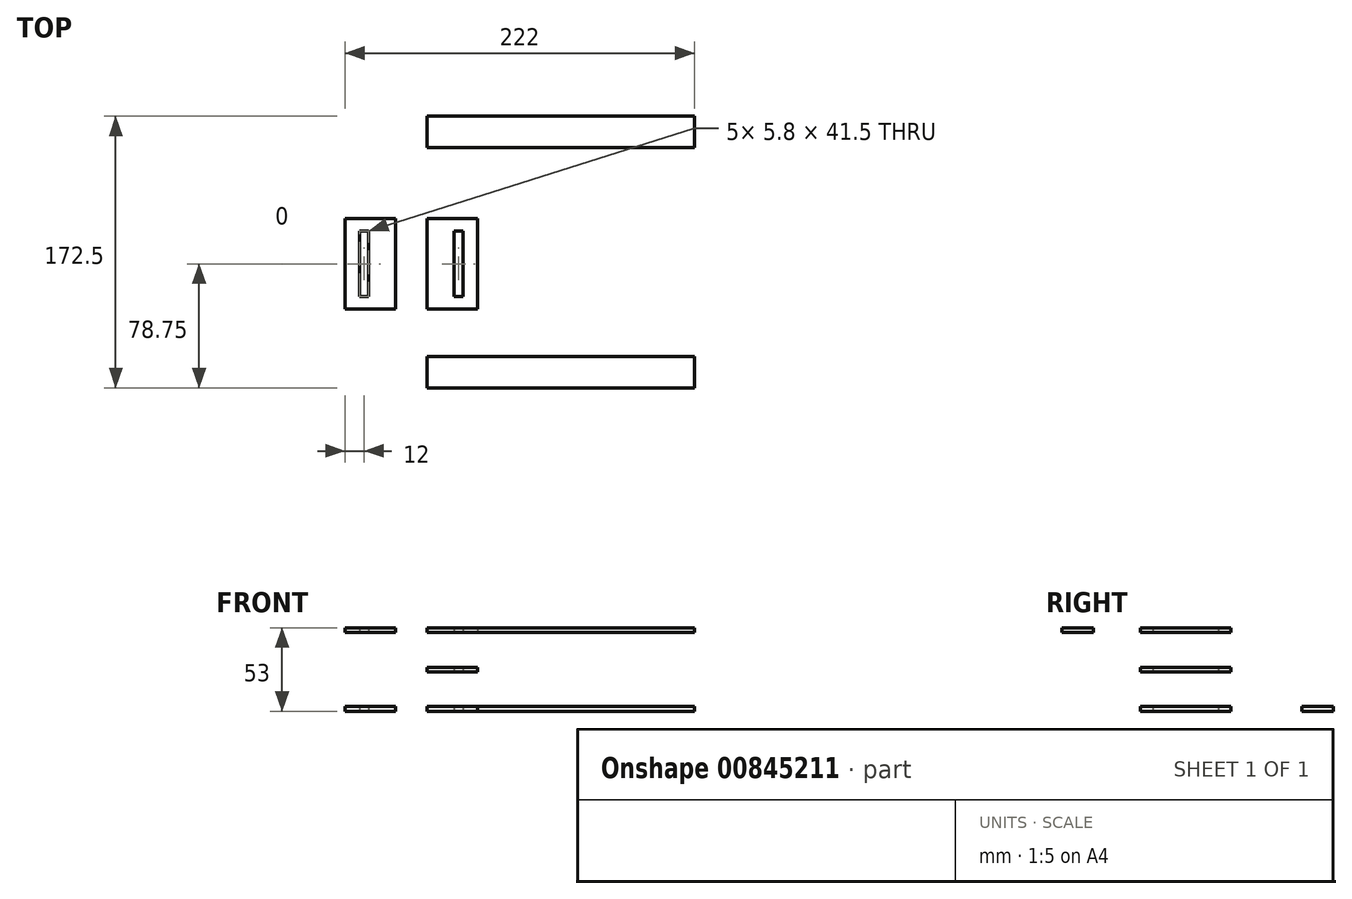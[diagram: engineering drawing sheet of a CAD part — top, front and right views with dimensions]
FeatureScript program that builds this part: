
annotation { "Feature Type Name" : "Feature", "Feature Type Description" : "" }
export const myFeature = defineFeature(function(context is Context, id is Id, definition is map)
    precondition{}
    {
        {
            var Q0;
            Q0=qCreatedBy(makeId("Top.planeOp"),FACE);
            var sketch = newSketch(context, id + "F0", { "sketchPlane" : qUnion([Q0])});
            skLineSegment(sketch, "E0.bottom", {"start": v(2.9, 20.75) * mm, "end": v(-2.9, 20.75) * mm});
            skLineSegment(sketch, "E0.top", {"start": v(2.9, -20.75) * mm, "end": v(-2.9, -20.75) * mm});
            skLineSegment(sketch, "E0.left", {"start": v(2.9, 20.75) * mm, "end": v(2.9, -20.75) * mm});
            skLineSegment(sketch, "E0.right", {"start": v(-2.9, 20.75) * mm, "end": v(-2.9, -20.75) * mm});
            skPoint(sketch, "E0.middle", {"position": v(0, 0) * mm});
            skLineSegment(sketch, "E1.top", {"start": v(-20, 28.75) * mm, "end": v(12, 28.75) * mm});
            skLineSegment(sketch, "E1.left", {"start": v(-20, -28.75) * mm, "end": v(-20, 28.75) * mm});
            skLineSegment(sketch, "E1.right", {"start": v(12, -28.75) * mm, "end": v(12, 28.75) * mm});
            skLineSegment(sketch, "E2.bottom", {"start": v(-20, -28.75) * mm, "end": v(12, -28.75) * mm});
            skSolve(sketch);
        }
        {
            var Q0;
            Q0=makeQuery(id+"F0.imprint","IMPRINT",FACE,{"disambiguationData":[TD([[makeQuery(id+"F0.imprint","IMPRINT",EDGE,{"derivedFrom":sQuery(id+"F0.wireOp",EDGE,"E0.bottom")}),-1.0]])]});
            var Q1;
            Q1=makeQuery(id+"F0.imprint","IMPRINT",FACE,{"disambiguationData":[TD([[makeQuery(id+"F0.imprint","IMPRINT",EDGE,{"derivedFrom":sQuery(id+"F0.wireOp",EDGE,"JnjF8kHf-qQj9-1dLX-JmeW-Ht2cM5oFc9sg.bottom")}),1.0]])]});
            var Q2;
            {var subQ0=sQuery(id+"F0.wireOp",EDGE,"E2.bottom");Q2=makeQuery(id+"F0.imprint","IMPRINT",FACE,{"disambiguationData":[TD([[makeQuery(id+"F0.imprint","IMPRINT",EDGE,{"derivedFrom":subQ0}),1.0]])]});}
            extrude(context, id + "F1", {"entities" : qUnion([Q0, Q1, Q2]), "depth" : 3 * mm, "offsetDistance" : 25 * mm});
        }
        {
            var Q0;
            Q0=qCreatedBy(makeId("Top.planeOp"),FACE);
            cPlane(context, id + "F2", {"entities" : qUnion([Q0]), "cplaneType" : CPlaneType.OFFSET, "offset" : 25 * mm, "width" : 150 * mm, "height" : 150 * mm});
        }
        {
            var Q0;
            Q0=qCreatedBy(id+"F2.planeOp",FACE);
            var sketch = newSketch(context, id + "F3", { "sketchPlane" : qUnion([Q0])});
            skLineSegment(sketch, "E3.0.0", {"start": v(-20, 28.75) * mm, "end": v(-20, -28.75) * mm});
            skLineSegment(sketch, "E3.0.1", {"start": v(-20, -28.75) * mm, "end": v(12, -28.75) * mm});
            skLineSegment(sketch, "E3.0.2", {"start": v(12, -28.75) * mm, "end": v(12, 28.75) * mm});
            skLineSegment(sketch, "E3.0.3", {"start": v(12, 28.75) * mm, "end": v(-20, 28.75) * mm});
            skLineSegment(sketch, "E4.0", {"start": v(-2.9, 20.75) * mm, "end": v(-2.9, -20.75) * mm});
            skLineSegment(sketch, "E4.1", {"start": v(2.9, 20.75) * mm, "end": v(-2.9, 20.75) * mm});
            skLineSegment(sketch, "E4.2", {"start": v(2.9, 20.75) * mm, "end": v(2.9, -20.75) * mm});
            skLineSegment(sketch, "E4.3", {"start": v(2.9, -20.75) * mm, "end": v(-2.9, -20.75) * mm});
            skLineSegment(sketch, "E5.bottom", {"start": v(-20, -28.75) * mm, "end": v(0, -28.75) * mm});
            skLineSegment(sketch, "E5.top", {"start": v(-20, -58.75) * mm, "end": v(0, -58.75) * mm});
            skLineSegment(sketch, "E5.left", {"start": v(-20, -28.75) * mm, "end": v(-20, -58.75) * mm});
            skLineSegment(sketch, "E5.right", {"start": v(0, -28.75) * mm, "end": v(0, -58.75) * mm});
            skLineSegment(sketch, "E6.bottom", {"start": v(-20, -58.75) * mm, "end": v(150, -58.75) * mm});
            skLineSegment(sketch, "E6.top", {"start": v(-20, -78.75) * mm, "end": v(150, -78.75) * mm});
            skLineSegment(sketch, "E6.left", {"start": v(-20, -58.75) * mm, "end": v(-20, -78.75) * mm});
            skLineSegment(sketch, "E6.right", {"start": v(150, -58.75) * mm, "end": v(150, -78.75) * mm});
            skLineSegment(sketch, "E7.bottom", {"start": v(-20, 28.75) * mm, "end": v(0, 28.75) * mm});
            skLineSegment(sketch, "E7.top", {"start": v(-20, 74.75) * mm, "end": v(0, 74.75) * mm});
            skLineSegment(sketch, "E7.left", {"start": v(-20, 28.75) * mm, "end": v(-20, 74.75) * mm});
            skLineSegment(sketch, "E7.right", {"start": v(0, 28.75) * mm, "end": v(0, 74.75) * mm});
            skSolve(sketch);
        }
        {
            var Q0;
            Q0=makeQuery(id+"F3.imprint","IMPRINT",FACE,{"disambiguationData":[TD([[makeQuery(id+"F3.imprint","IMPRINT",EDGE,{"derivedFrom":sQuery(id+"F3.wireOp",EDGE,"E3.0.0")}),1.0]])]});
            var Q1;
            Q1=makeQuery(id+"F3.imprint","IMPRINT",FACE,{"disambiguationData":[TD([[makeQuery(id+"F3.imprint","IMPRINT",EDGE,{"derivedFrom":sQuery(id+"F3.wireOp",EDGE,"E5.bottom")}),-1.0]])]});
            var Q2;
            Q2=makeQuery(id+"F3.imprint","IMPRINT",FACE,{"disambiguationData":[TD([[makeQuery(id+"F3.imprint","IMPRINT",EDGE,{"derivedFrom":sQuery(id+"F3.wireOp",EDGE,"E6.top")}),1.0]])]});
            var Q3;
            Q3=makeQuery(id+"F3.imprint","IMPRINT",FACE,{"disambiguationData":[TD([[makeQuery(id+"F3.imprint","IMPRINT",EDGE,{"derivedFrom":sQuery(id+"F3.wireOp",EDGE,"E7.bottom")}),1.0]])]});
            extrude(context, id + "F4", {"entities" : qUnion([Q0, Q1, Q2, Q3]), "depth" : 3 * mm, "offsetDistance" : 25 * mm});
        }
        {
            var Q0;
            Q0=qCreatedBy(makeId("Right.planeOp"),FACE);
            cPlane(context, id + "F5", {"entities" : qUnion([Q0]), "cplaneType" : CPlaneType.OFFSET, "offset" : 30 * mm, "oppositeDirection" : true, "width" : 150 * mm, "height" : 150 * mm});
        }
        {
            var Q0;
            Q0=makeQuery(id+"F4.opExtrude","SWEPT_BODY",BODY,{"disambiguationData":[OSD([sQuery(id+"F3.wireOp",EDGE,"E3.0.0"),sQuery(id+"F3.wireOp",EDGE,"E3.0.1"),sQuery(id+"F3.wireOp",EDGE,"E3.0.2"),sQuery(id+"F3.wireOp",EDGE,"E3.0.3"),sQuery(id+"F3.wireOp",EDGE,"E4.0"),sQuery(id+"F3.wireOp",EDGE,"E4.1"),sQuery(id+"F3.wireOp",EDGE,"E4.2"),sQuery(id+"F3.wireOp",EDGE,"E4.3"),sQuery(id+"F3.wireOp",EDGE,"E5.left"),sQuery(id+"F3.wireOp",EDGE,"E5.right"),sQuery(id+"F3.wireOp",EDGE,"E6.bottom"),sQuery(id+"F3.wireOp",EDGE,"E6.top"),sQuery(id+"F3.wireOp",EDGE,"E6.left"),sQuery(id+"F3.wireOp",EDGE,"E6.right"),sQuery(id+"F3.wireOp",EDGE,"E7.top"),sQuery(id+"F3.wireOp",EDGE,"E7.left"),sQuery(id+"F3.wireOp",EDGE,"E7.right")])]});
            var Q1;
            Q1=qCreatedBy(id+"F5.planeOp",FACE);
            mirror(context, id + "F6", {"entities" : qUnion([Q0]), "mirrorPlane" : qUnion([Q1])});
        }
        {
            var Q0;
            Q0=makeQuery(id+"F6.opPattern","COPY",FACE,{"derivedFrom":makeQuery(id+"F4.opExtrude","CAP_FACE",FACE,{"disambiguationData":[OSD([sQuery(id+"F3.wireOp",EDGE,"E3.0.0"),sQuery(id+"F3.wireOp",EDGE,"E3.0.1"),sQuery(id+"F3.wireOp",EDGE,"E3.0.2"),sQuery(id+"F3.wireOp",EDGE,"E3.0.3"),sQuery(id+"F3.wireOp",EDGE,"E4.0"),sQuery(id+"F3.wireOp",EDGE,"E4.1"),sQuery(id+"F3.wireOp",EDGE,"E4.2"),sQuery(id+"F3.wireOp",EDGE,"E4.3"),sQuery(id+"F3.wireOp",EDGE,"E5.left"),sQuery(id+"F3.wireOp",EDGE,"E5.right"),sQuery(id+"F3.wireOp",EDGE,"E6.bottom"),sQuery(id+"F3.wireOp",EDGE,"E6.top"),sQuery(id+"F3.wireOp",EDGE,"E6.left"),sQuery(id+"F3.wireOp",EDGE,"E6.right"),sQuery(id+"F3.wireOp",EDGE,"E7.top"),sQuery(id+"F3.wireOp",EDGE,"E7.left"),sQuery(id+"F3.wireOp",EDGE,"E7.right")])],"isStart":true}),"instanceName":"1"});
            var sketch = newSketch(context, id + "F7", { "sketchPlane" : qUnion([Q0])});
            skSolve(sketch);
        }
        {
            var Q0;
            Q0=qCreatedBy(makeId("Top.planeOp"),FACE);
            cPlane(context, id + "F8", {"entities" : qUnion([Q0]), "cplaneType" : CPlaneType.OFFSET, "offset" : 25 * mm, "oppositeDirection" : true, "width" : 150 * mm, "height" : 150 * mm});
        }
        {
            var Q0;
            Q0=qCreatedBy(id+"F8.planeOp",FACE);
            var sketch = newSketch(context, id + "F9", { "sketchPlane" : qUnion([Q0])});
            skLineSegment(sketch, "E8.0", {"start": v(-20, -28.75) * mm, "end": v(-20, 28.75) * mm});
            skLineSegment(sketch, "E8.1", {"start": v(-20, 28.75) * mm, "end": v(12, 28.75) * mm});
            skLineSegment(sketch, "E8.2", {"start": v(-20, -28.75) * mm, "end": v(12, -28.75) * mm});
            skLineSegment(sketch, "E8.3", {"start": v(2.9, -20.75) * mm, "end": v(-2.9, -20.75) * mm});
            skLineSegment(sketch, "E8.4", {"start": v(-2.9, 20.75) * mm, "end": v(-2.9, -20.75) * mm});
            skLineSegment(sketch, "E8.5", {"start": v(2.9, 20.75) * mm, "end": v(2.9, -20.75) * mm});
            skLineSegment(sketch, "E8.6", {"start": v(2.9, 20.75) * mm, "end": v(-2.9, 20.75) * mm});
            skLineSegment(sketch, "E9.0", {"start": v(12, -28.75) * mm, "end": v(12, 28.75) * mm});
            skLineSegment(sketch, "E10.bottom", {"start": v(-20, -28.75) * mm, "end": v(0, -28.75) * mm});
            skLineSegment(sketch, "E10.top", {"start": v(-20, -74.75) * mm, "end": v(0, -74.75) * mm});
            skLineSegment(sketch, "E10.left", {"start": v(-20, -28.75) * mm, "end": v(-20, -74.75) * mm});
            skLineSegment(sketch, "E10.right", {"start": v(0, -28.75) * mm, "end": v(0, -74.75) * mm});
            skLineSegment(sketch, "E11.bottom", {"start": v(-20, 28.75) * mm, "end": v(0, 28.75) * mm});
            skLineSegment(sketch, "E11.top", {"start": v(-20, 73.75) * mm, "end": v(0, 73.75) * mm});
            skLineSegment(sketch, "E11.left", {"start": v(-20, 28.75) * mm, "end": v(-20, 73.75) * mm});
            skLineSegment(sketch, "E11.right", {"start": v(0, 28.75) * mm, "end": v(0, 73.75) * mm});
            skLineSegment(sketch, "E12.bottom", {"start": v(-20, 73.75) * mm, "end": v(150, 73.75) * mm});
            skLineSegment(sketch, "E12.top", {"start": v(-20, 93.75) * mm, "end": v(150, 93.75) * mm});
            skLineSegment(sketch, "E12.left", {"start": v(-20, 73.75) * mm, "end": v(-20, 93.75) * mm});
            skLineSegment(sketch, "E12.right", {"start": v(150, 73.75) * mm, "end": v(150, 93.75) * mm});
            skSolve(sketch);
        }
        {
            var Q0;
            Q0=makeQuery(id+"F9.imprint","IMPRINT",FACE,{"disambiguationData":[TD([[makeQuery(id+"F9.imprint","IMPRINT",EDGE,{"derivedFrom":sQuery(id+"F9.wireOp",EDGE,"E12.top")}),-1.0]])]});
            var Q1;
            Q1=makeQuery(id+"F9.imprint","IMPRINT",FACE,{"disambiguationData":[TD([[makeQuery(id+"F9.imprint","IMPRINT",EDGE,{"derivedFrom":sQuery(id+"F9.wireOp",EDGE,"E11.bottom")}),1.0]])]});
            var Q2;
            Q2=makeQuery(id+"F9.imprint","IMPRINT",FACE,{"disambiguationData":[TD([[makeQuery(id+"F9.imprint","IMPRINT",EDGE,{"derivedFrom":sQuery(id+"F9.wireOp",EDGE,"E8.0")}),-1.0]])]});
            var Q3;
            Q3=makeQuery(id+"F9.imprint","IMPRINT",FACE,{"disambiguationData":[TD([[makeQuery(id+"F9.imprint","IMPRINT",EDGE,{"derivedFrom":sQuery(id+"F9.wireOp",EDGE,"E10.bottom")}),-1.0]])]});
            extrude(context, id + "F10", {"entities" : qUnion([Q0, Q1, Q2, Q3]), "depth" : 3 * mm, "offsetDistance" : 25 * mm});
        }
        {
            var Q0;
            Q0=makeQuery(id+"F10.opExtrude","SWEPT_BODY",BODY,{"disambiguationData":[OSD([sQuery(id+"F9.wireOp",EDGE,"E8.0"),sQuery(id+"F9.wireOp",EDGE,"E8.1"),sQuery(id+"F9.wireOp",EDGE,"E8.2"),sQuery(id+"F9.wireOp",EDGE,"E8.3"),sQuery(id+"F9.wireOp",EDGE,"E8.4"),sQuery(id+"F9.wireOp",EDGE,"E8.5"),sQuery(id+"F9.wireOp",EDGE,"E8.6"),sQuery(id+"F9.wireOp",EDGE,"E9.0"),sQuery(id+"F9.wireOp",EDGE,"E10.top"),sQuery(id+"F9.wireOp",EDGE,"E10.left"),sQuery(id+"F9.wireOp",EDGE,"E10.right"),sQuery(id+"F9.wireOp",EDGE,"E11.left"),sQuery(id+"F9.wireOp",EDGE,"E11.right"),sQuery(id+"F9.wireOp",EDGE,"E12.bottom"),sQuery(id+"F9.wireOp",EDGE,"E12.top"),sQuery(id+"F9.wireOp",EDGE,"E12.left"),sQuery(id+"F9.wireOp",EDGE,"E12.right")])]});
            var Q1;
            Q1=qCreatedBy(id+"F5.planeOp",FACE);
            mirror(context, id + "F11", {"entities" : qUnion([Q0]), "mirrorPlane" : qUnion([Q1])});
        }
        {
            var Q0;
            Q0=makeQuery(id+"F11.opPattern","COPY",FACE,{"derivedFrom":makeQuery(id+"F10.opExtrude","CAP_FACE",FACE,{"disambiguationData":[OSD([sQuery(id+"F9.wireOp",EDGE,"E8.0"),sQuery(id+"F9.wireOp",EDGE,"E8.1"),sQuery(id+"F9.wireOp",EDGE,"E8.2"),sQuery(id+"F9.wireOp",EDGE,"E8.3"),sQuery(id+"F9.wireOp",EDGE,"E8.4"),sQuery(id+"F9.wireOp",EDGE,"E8.5"),sQuery(id+"F9.wireOp",EDGE,"E8.6"),sQuery(id+"F9.wireOp",EDGE,"E9.0"),sQuery(id+"F9.wireOp",EDGE,"E10.top"),sQuery(id+"F9.wireOp",EDGE,"E10.left"),sQuery(id+"F9.wireOp",EDGE,"E10.right"),sQuery(id+"F9.wireOp",EDGE,"E11.left"),sQuery(id+"F9.wireOp",EDGE,"E11.right"),sQuery(id+"F9.wireOp",EDGE,"E12.bottom"),sQuery(id+"F9.wireOp",EDGE,"E12.top"),sQuery(id+"F9.wireOp",EDGE,"E12.left"),sQuery(id+"F9.wireOp",EDGE,"E12.right")])],"isStart":true}),"instanceName":"1"});
            var sketch = newSketch(context, id + "F12", { "sketchPlane" : qUnion([Q0])});
            skSolve(sketch);
        }
    });
